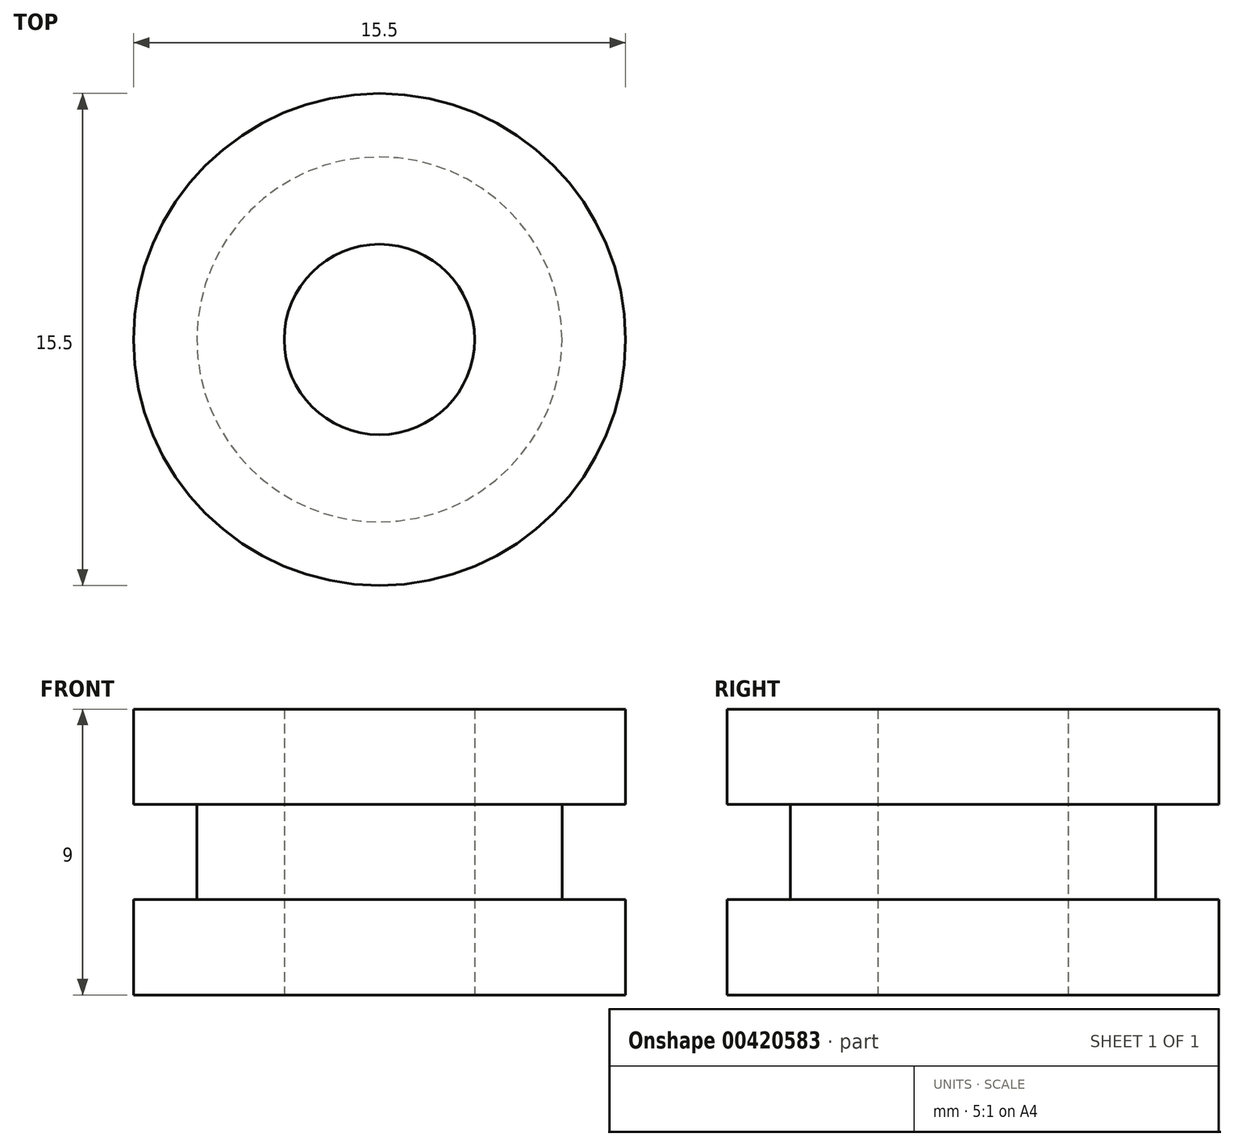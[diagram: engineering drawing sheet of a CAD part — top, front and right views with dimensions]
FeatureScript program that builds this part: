
annotation { "Feature Type Name" : "Feature", "Feature Type Description" : "" }
export const myFeature = defineFeature(function(context is Context, id is Id, definition is map)
    precondition{}
    {
        {
            var Q0;
            Q0=qCreatedBy(makeId("Front.planeOp"),FACE);
            var sketch = newSketch(context, id + "F0", { "sketchPlane" : qUnion([Q0])});
            skLineSegment(sketch, "E0", {"start": v(0, -4.5) * mm, "end": v(0, 4.5) * mm, "construction": true});
            skLineSegment(sketch, "E1", {"start": v(-3, -4.5) * mm, "end": v(-3, 4.5) * mm});
            skLineSegment(sketch, "E2", {"start": v(-3, 4.5) * mm, "end": v(-7.75, 4.5) * mm});
            skLineSegment(sketch, "E3", {"start": v(-7.75, 4.5) * mm, "end": v(-7.75, 1.5) * mm});
            skLineSegment(sketch, "E4", {"start": v(-7.75, 1.5) * mm, "end": v(-5.75, 1.5) * mm});
            skLineSegment(sketch, "E5", {"start": v(-5.75, 1.5) * mm, "end": v(-5.75, -1.5) * mm});
            skLineSegment(sketch, "E6", {"start": v(-5.75, -1.5) * mm, "end": v(-7.75, -1.5) * mm});
            skLineSegment(sketch, "E7", {"start": v(-7.75, -1.5) * mm, "end": v(-7.75, -4.5) * mm});
            skLineSegment(sketch, "E8", {"start": v(-7.75, -4.5) * mm, "end": v(-3, -4.5) * mm});
            skLineSegment(sketch, "E9", {"start": v(-5.75, 0) * mm, "end": v(0, 0) * mm, "construction": true});
            skSolve(sketch);
        }
        {
            var Q0;
            Q0 = qSketchRegion(id + "F0", true);
            var Q1;
            Q1=sQuery(id+"F0.wireOp",EDGE,"E0");
            revolve(context, id + "F1", {"surfaceOperationType" : NewSurfaceOperationType.NEW, "entities" : qUnion([Q0]), "axis" : qUnion([Q1]), "revolveType" : RevolveType.FULL});
        }
    });
